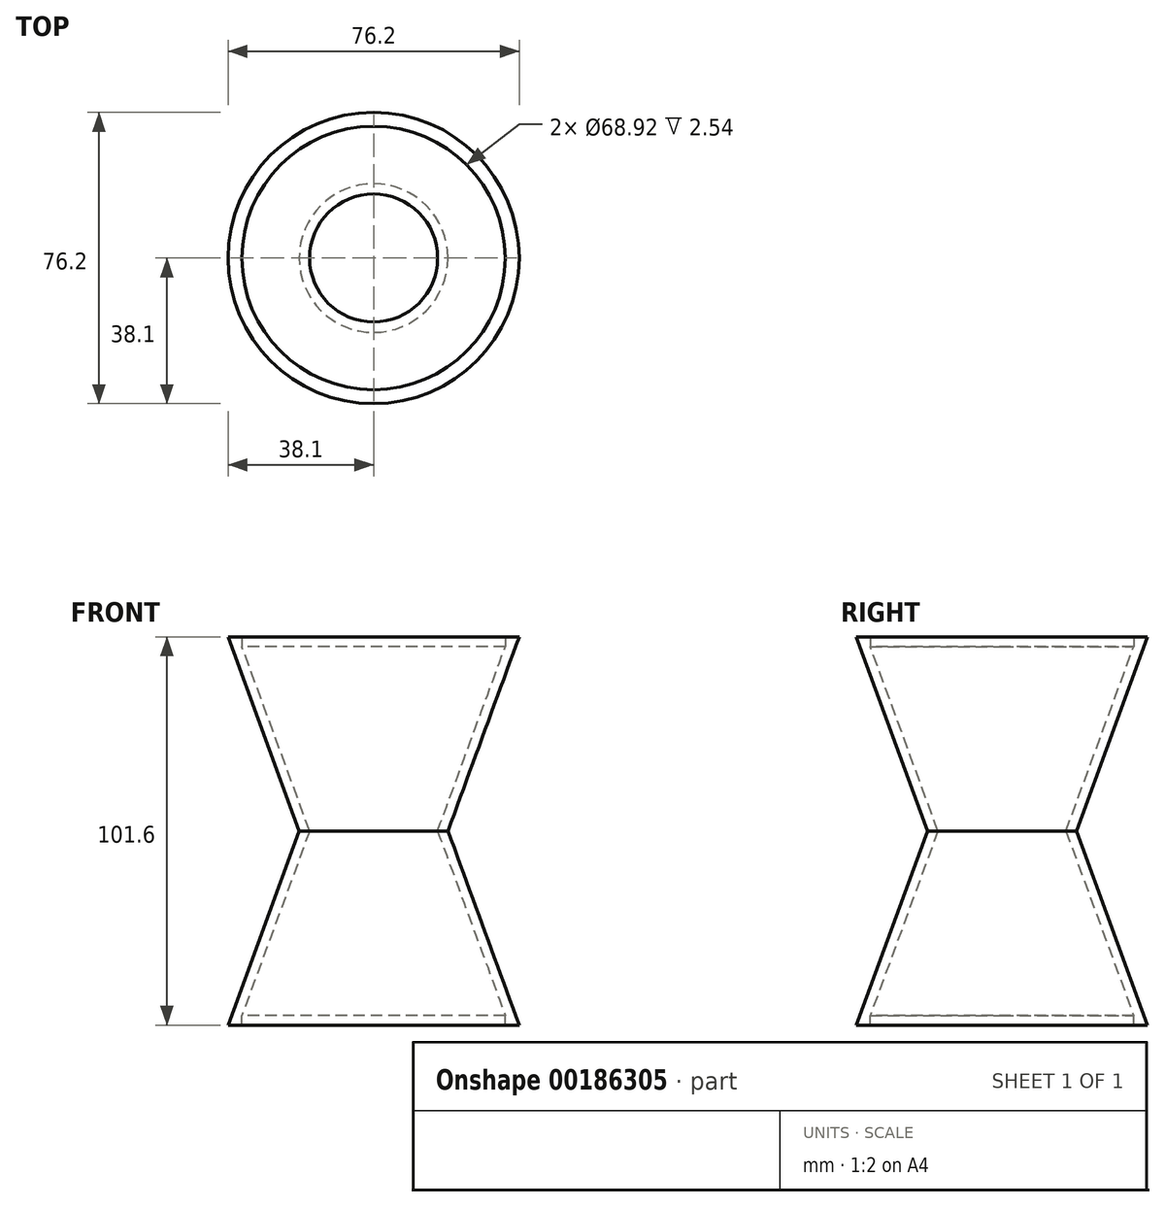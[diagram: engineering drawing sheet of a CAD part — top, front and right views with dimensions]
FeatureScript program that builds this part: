
annotation { "Feature Type Name" : "Feature", "Feature Type Description" : "" }
export const myFeature = defineFeature(function(context is Context, id is Id, definition is map)
    precondition{}
    {
        {
            var Q0;
            Q0=qCreatedBy(makeId("Top.planeOp"),FACE);
            var sketch = newSketch(context, id + "F0", { "sketchPlane" : qUnion([Q0])});
            skCircle(sketch, "E0", {"center": v(0, 0) * mm, "radius": 38.1 * mm});
            skSolve(sketch);
        }
        {
            var Q0;
            Q0=qCreatedBy(makeId("Top.planeOp"),FACE);
            cPlane(context, id + "F1", {"entities" : qUnion([Q0]), "cplaneType" : CPlaneType.OFFSET, "offset" : 50.8 * mm, "width" : 152.4 * mm, "height" : 152.4 * mm});
        }
        {
            var Q0;
            Q0=qCreatedBy(id+"F1.planeOp",FACE);
            var sketch = newSketch(context, id + "F2", { "sketchPlane" : qUnion([Q0])});
            skCircle(sketch, "E1", {"center": v(0, 0) * mm, "radius": 19.46 * mm});
            skSolve(sketch);
        }
        {
            var Q0;
            Q0=makeQuery(id+"F0.imprint","IMPRINT",FACE,{"disambiguationData":[TD([[makeQuery(id+"F0.imprint","IMPRINT",EDGE,{"derivedFrom":sQuery(id+"F0.wireOp",EDGE,"E0")}),1.0]])]});
            var Q1;
            Q1=makeQuery(id+"F2.imprint","IMPRINT",FACE,{"disambiguationData":[TD([[makeQuery(id+"F2.imprint","IMPRINT",EDGE,{"derivedFrom":sQuery(id+"F2.wireOp",EDGE,"E1")}),1.0]])]});
            loft(context, id + "F3", {"sheetProfilesArray" : [{ "sheetProfileEntities" : qUnion([Q0]) }, { "sheetProfileEntities" : qUnion([Q1]) }]});
        }
        {
            var Q0;
            Q0=makeQuery(id+"F3.opLoft","CAP_FACE",FACE,{"disambiguationData":[OSD([makeQuery(id+"F2.imprint","IMPRINT",FACE,{"disambiguationData":[TD([[makeQuery(id+"F2.imprint","IMPRINT",EDGE,{"derivedFrom":sQuery(id+"F2.wireOp",EDGE,"E1")}),1.0]])]})])],"isStart":true});
            shell(context, id + "F4", {"entities" : qUnion([Q0]), "thickness" : 2.54 * mm});
        }
        {
            var Q0;
            Q0=makeQuery(id+"F4.opShell","OFFSET_FACE",FACE,{"disambiguationData":[OSD([makeQuery(id+"F0.imprint","IMPRINT",FACE,{"disambiguationData":[TD([[makeQuery(id+"F0.imprint","IMPRINT",EDGE,{"derivedFrom":sQuery(id+"F0.wireOp",EDGE,"E0")}),1.0]])]})])]});
            extrude(context, id + "F5", {"entities" : qUnion([Q0]), "operationType" : NewBodyOperationType.REMOVE, "oppositeDirection" : true, "depth" : 25.4 * mm});
        }
        {
            var Q0;
            Q0=makeQuery(id+"F3.opLoft","SWEPT_BODY",BODY,{"disambiguationData":[OSD([makeQuery(id+"F0.imprint","IMPRINT",FACE,{"disambiguationData":[TD([[makeQuery(id+"F0.imprint","IMPRINT",EDGE,{"derivedFrom":sQuery(id+"F0.wireOp",EDGE,"E0")}),1.0]])]}),makeQuery(id+"F2.imprint","IMPRINT",FACE,{"disambiguationData":[TD([[makeQuery(id+"F2.imprint","IMPRINT",EDGE,{"derivedFrom":sQuery(id+"F2.wireOp",EDGE,"E1")}),1.0]])]})])]});
            var Q1;
            Q1=qCreatedBy(id+"F1.planeOp",FACE);
            mirror(context, id + "F6", {"operationType" : NewBodyOperationType.ADD, "entities" : qUnion([Q0]), "mirrorPlane" : qUnion([Q1])});
        }
    });
